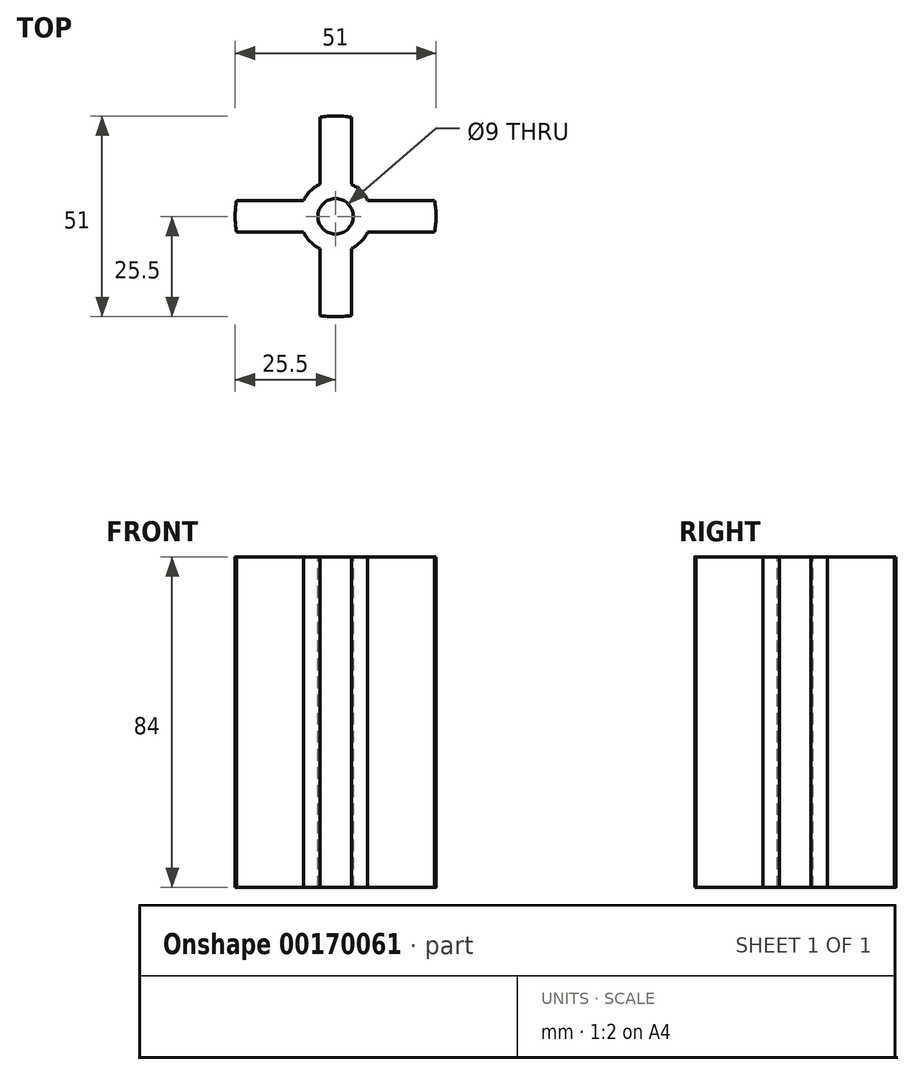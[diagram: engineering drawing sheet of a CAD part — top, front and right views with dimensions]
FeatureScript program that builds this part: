
annotation { "Feature Type Name" : "Feature", "Feature Type Description" : "" }
export const myFeature = defineFeature(function(context is Context, id is Id, definition is map)
    precondition{}
    {
        {
            var Q0;
            Q0=qCreatedBy(makeId("Top.planeOp"),FACE);
            var sketch = newSketch(context, id + "F0", { "sketchPlane" : qUnion([Q0])});
            skCircle(sketch, "E0", {"center": v(0, 0) * mm, "radius": 11.1 * mm});
            skCircle(sketch, "E1.0", {"center": v(0, 0) * mm, "radius": 13.1 * mm});
            skCircle(sketch, "E2.0", {"center": v(0, 0) * mm, "radius": 9.1 * mm});
            skCircle(sketch, "E3", {"center": v(0, 0) * mm, "radius": 25.5 * mm});
            skLineSegment(sketch, "E4.bottom", {"start": v(-4, -25.18) * mm, "end": v(4, -25.18) * mm});
            skLineSegment(sketch, "E4.top", {"start": v(-4, 25.18) * mm, "end": v(4, 25.18) * mm});
            skLineSegment(sketch, "E4.left", {"start": v(-4, -25.18) * mm, "end": v(-4, 25.18) * mm});
            skLineSegment(sketch, "E4.right", {"start": v(4, -25.18) * mm, "end": v(4, 25.18) * mm});
            skLineSegment(sketch, "E5.bottom", {"start": v(-25.18, -4) * mm, "end": v(25.18, -4) * mm});
            skLineSegment(sketch, "E5.top", {"start": v(-25.18, 4) * mm, "end": v(25.18, 4) * mm});
            skLineSegment(sketch, "E5.left", {"start": v(-25.18, -4) * mm, "end": v(-25.18, 4) * mm});
            skLineSegment(sketch, "E5.right", {"start": v(25.18, -4) * mm, "end": v(25.18, 4) * mm});
            skCircle(sketch, "E6", {"center": v(0, 0) * mm, "radius": 4.5 * mm});
            skSolve(sketch);
        }
        {
            var Q0;
            {var subQ5=sQuery(id+"F0.wireOp",EDGE,"E4.top");Q0=makeQuery(id+"F0.imprint","IMPRINT",FACE,{"disambiguationData":[TD([[makeQuery(id+"F0.imprint","IMPRINT",EDGE,{"derivedFrom":subQ5}),-1.0]])]});}
            var Q1;
            {var subQ0=sQuery(id+"F0.wireOp",EDGE,"E4.top");Q1=makeQuery(id+"F0.imprint","IMPRINT",FACE,{"disambiguationData":[TD([[makeQuery(id+"F0.imprint","IMPRINT",EDGE,{"derivedFrom":subQ0}),1.0]])]});}
            var Q2;
            {var subQ0=sQuery(id+"F0.wireOp",EDGE,"E5.right");Q2=makeQuery(id+"F0.imprint","IMPRINT",FACE,{"disambiguationData":[TD([[makeQuery(id+"F0.imprint","IMPRINT",EDGE,{"derivedFrom":subQ0}),-1.0]])]});}
            var Q3;
            {var subQ5=sQuery(id+"F0.wireOp",EDGE,"E5.right");Q3=makeQuery(id+"F0.imprint","IMPRINT",FACE,{"disambiguationData":[TD([[makeQuery(id+"F0.imprint","IMPRINT",EDGE,{"derivedFrom":subQ5}),1.0]])]});}
            var Q4;
            {var subQ0=sQuery(id+"F0.wireOp",EDGE,"E4.bottom");Q4=makeQuery(id+"F0.imprint","IMPRINT",FACE,{"disambiguationData":[TD([[makeQuery(id+"F0.imprint","IMPRINT",EDGE,{"derivedFrom":subQ0}),-1.0]])]});}
            var Q5;
            {var subQ0=sQuery(id+"F0.wireOp",EDGE,"E5.left");Q5=makeQuery(id+"F0.imprint","IMPRINT",FACE,{"disambiguationData":[TD([[makeQuery(id+"F0.imprint","IMPRINT",EDGE,{"derivedFrom":subQ0}),1.0]])]});}
            var Q6;
            {var subQ5=sQuery(id+"F0.wireOp",EDGE,"E5.left");Q6=makeQuery(id+"F0.imprint","IMPRINT",FACE,{"disambiguationData":[TD([[makeQuery(id+"F0.imprint","IMPRINT",EDGE,{"derivedFrom":subQ5}),-1.0]])]});}
            var Q7;
            {var subQ5=sQuery(id+"F0.wireOp",EDGE,"E4.bottom");Q7=makeQuery(id+"F0.imprint","IMPRINT",FACE,{"disambiguationData":[TD([[makeQuery(id+"F0.imprint","IMPRINT",EDGE,{"derivedFrom":subQ5}),1.0]])]});}
            var Q8;
            {var subQ0=sQuery(id+"F0.wireOp",EDGE,"E5.top");var subQ1=sQuery(id+"F0.wireOp",EDGE,"E0");var subQ2=makeQuery(id+"F0.imprint","INTERSECT",VERTEX,{"disambiguationData":[OD(1.0)],"derivedFrom":[subQ1,subQ0]});Q8=makeQuery(id+"F0.imprint","IMPRINT",FACE,{"disambiguationData":[TD([[makeQuery(id+"F0.imprint","IMPRINT",EDGE,{"disambiguationData":[TD([[subQ2,-1.0]])],"derivedFrom":subQ1}),1.0]])]});}
            var Q9;
            {var subQ0=sQuery(id+"F0.wireOp",EDGE,"E5.top");var subQ1=sQuery(id+"F0.wireOp",EDGE,"E0");var subQ2=makeQuery(id+"F0.imprint","INTERSECT",VERTEX,{"disambiguationData":[OD(1.0)],"derivedFrom":[subQ1,subQ0]});Q9=makeQuery(id+"F0.imprint","IMPRINT",FACE,{"disambiguationData":[TD([[makeQuery(id+"F0.imprint","IMPRINT",EDGE,{"disambiguationData":[TD([[subQ2,-1.0]])],"derivedFrom":subQ1}),-1.0]])]});}
            var Q10;
            {var subQ0=sQuery(id+"F0.wireOp",EDGE,"E4.right");var subQ1=sQuery(id+"F0.wireOp",EDGE,"E0");var subQ2=makeQuery(id+"F0.imprint","INTERSECT",VERTEX,{"disambiguationData":[OD(0.0)],"derivedFrom":[subQ1,subQ0]});Q10=makeQuery(id+"F0.imprint","IMPRINT",FACE,{"disambiguationData":[TD([[makeQuery(id+"F0.imprint","IMPRINT",EDGE,{"disambiguationData":[TD([[subQ2,-1.0]])],"derivedFrom":subQ1}),1.0]])]});}
            var Q11;
            {var subQ0=sQuery(id+"F0.wireOp",EDGE,"E4.right");var subQ1=sQuery(id+"F0.wireOp",EDGE,"E0");var subQ2=makeQuery(id+"F0.imprint","INTERSECT",VERTEX,{"disambiguationData":[OD(0.0)],"derivedFrom":[subQ1,subQ0]});Q11=makeQuery(id+"F0.imprint","IMPRINT",FACE,{"disambiguationData":[TD([[makeQuery(id+"F0.imprint","IMPRINT",EDGE,{"disambiguationData":[TD([[subQ2,-1.0]])],"derivedFrom":subQ1}),-1.0]])]});}
            var Q12;
            {var subQ0=sQuery(id+"F0.wireOp",EDGE,"E5.top");var subQ1=sQuery(id+"F0.wireOp",EDGE,"E0");var subQ2=makeQuery(id+"F0.imprint","INTERSECT",VERTEX,{"disambiguationData":[OD(0.0)],"derivedFrom":[subQ1,subQ0]});Q12=makeQuery(id+"F0.imprint","IMPRINT",FACE,{"disambiguationData":[TD([[makeQuery(id+"F0.imprint","IMPRINT",EDGE,{"disambiguationData":[TD([[subQ2,1.0]])],"derivedFrom":subQ1}),-1.0]])]});}
            var Q13;
            {var subQ0=sQuery(id+"F0.wireOp",EDGE,"E5.top");var subQ1=sQuery(id+"F0.wireOp",EDGE,"E0");var subQ2=makeQuery(id+"F0.imprint","INTERSECT",VERTEX,{"disambiguationData":[OD(0.0)],"derivedFrom":[subQ1,subQ0]});Q13=makeQuery(id+"F0.imprint","IMPRINT",FACE,{"disambiguationData":[TD([[makeQuery(id+"F0.imprint","IMPRINT",EDGE,{"disambiguationData":[TD([[subQ2,1.0]])],"derivedFrom":subQ1}),1.0]])]});}
            var Q14;
            {var subQ0=sQuery(id+"F0.wireOp",EDGE,"E4.left");var subQ1=sQuery(id+"F0.wireOp",EDGE,"E0");var subQ2=makeQuery(id+"F0.imprint","INTERSECT",VERTEX,{"disambiguationData":[OD(1.0)],"derivedFrom":[subQ1,subQ0]});Q14=makeQuery(id+"F0.imprint","IMPRINT",FACE,{"disambiguationData":[TD([[makeQuery(id+"F0.imprint","IMPRINT",EDGE,{"disambiguationData":[TD([[subQ2,-1.0]])],"derivedFrom":subQ1}),1.0]])]});}
            var Q15;
            {var subQ0=sQuery(id+"F0.wireOp",EDGE,"E4.left");var subQ1=sQuery(id+"F0.wireOp",EDGE,"E0");var subQ2=makeQuery(id+"F0.imprint","INTERSECT",VERTEX,{"disambiguationData":[OD(1.0)],"derivedFrom":[subQ1,subQ0]});Q15=makeQuery(id+"F0.imprint","IMPRINT",FACE,{"disambiguationData":[TD([[makeQuery(id+"F0.imprint","IMPRINT",EDGE,{"disambiguationData":[TD([[subQ2,-1.0]])],"derivedFrom":subQ1}),-1.0]])]});}
            var Q16;
            {var subQ3=sQuery(id+"F0.wireOp",EDGE,"E5.top");var subQ8=sQuery(id+"F0.wireOp",EDGE,"E2.0");var subQ10=makeQuery(id+"F0.imprint","INTERSECT",VERTEX,{"disambiguationData":[OD(1.0)],"derivedFrom":[subQ8,subQ3]});Q16=makeQuery(id+"F0.imprint","IMPRINT",FACE,{"disambiguationData":[TD([[makeQuery(id+"F0.imprint","IMPRINT",EDGE,{"disambiguationData":[TD([[subQ10,-1.0]])],"derivedFrom":subQ8}),1.0]])]});}
            var Q17;
            {var subQ0=sQuery(id+"F0.wireOp",EDGE,"E4.left");var subQ1=sQuery(id+"F0.wireOp",EDGE,"E2.0");var subQ2=makeQuery(id+"F0.imprint","INTERSECT",VERTEX,{"disambiguationData":[OD(0.0)],"derivedFrom":[subQ1,subQ0]});Q17=makeQuery(id+"F0.imprint","IMPRINT",FACE,{"disambiguationData":[TD([[makeQuery(id+"F0.imprint","IMPRINT",EDGE,{"disambiguationData":[TD([[subQ2,-1.0]])],"derivedFrom":subQ1}),1.0]])]});}
            var Q18;
            {var subQ5=sQuery(id+"F0.wireOp",EDGE,"E2.0");var subQ7=sQuery(id+"F0.wireOp",EDGE,"E4.right");var subQ8=makeQuery(id+"F0.imprint","INTERSECT",VERTEX,{"disambiguationData":[OD(0.0)],"derivedFrom":[subQ5,subQ7]});Q18=makeQuery(id+"F0.imprint","IMPRINT",FACE,{"disambiguationData":[TD([[makeQuery(id+"F0.imprint","IMPRINT",EDGE,{"disambiguationData":[TD([[subQ8,-1.0]])],"derivedFrom":subQ5}),1.0]])]});}
            var Q19;
            {var subQ0=sQuery(id+"F0.wireOp",EDGE,"E4.right");var subQ1=sQuery(id+"F0.wireOp",EDGE,"E2.0");var subQ2=makeQuery(id+"F0.imprint","INTERSECT",VERTEX,{"disambiguationData":[OD(0.0)],"derivedFrom":[subQ1,subQ0]});Q19=makeQuery(id+"F0.imprint","IMPRINT",FACE,{"disambiguationData":[TD([[makeQuery(id+"F0.imprint","IMPRINT",EDGE,{"disambiguationData":[TD([[subQ2,1.0]])],"derivedFrom":subQ1}),1.0]])]});}
            var Q20;
            {var subQ3=sQuery(id+"F0.wireOp",EDGE,"E5.top");var subQ8=sQuery(id+"F0.wireOp",EDGE,"E2.0");var subQ10=makeQuery(id+"F0.imprint","INTERSECT",VERTEX,{"disambiguationData":[OD(0.0)],"derivedFrom":[subQ8,subQ3]});Q20=makeQuery(id+"F0.imprint","IMPRINT",FACE,{"disambiguationData":[TD([[makeQuery(id+"F0.imprint","IMPRINT",EDGE,{"disambiguationData":[TD([[subQ10,1.0]])],"derivedFrom":subQ8}),1.0]])]});}
            var Q21;
            {var subQ1=sQuery(id+"F0.wireOp",EDGE,"E4.left");var subQ6=sQuery(id+"F0.wireOp",EDGE,"E2.0");var subQ9=makeQuery(id+"F0.imprint","INTERSECT",VERTEX,{"disambiguationData":[OD(1.0)],"derivedFrom":[subQ6,subQ1]});Q21=makeQuery(id+"F0.imprint","IMPRINT",FACE,{"disambiguationData":[TD([[makeQuery(id+"F0.imprint","IMPRINT",EDGE,{"disambiguationData":[TD([[subQ9,-1.0]])],"derivedFrom":subQ6}),1.0]])]});}
            var Q22;
            {var subQ0=sQuery(id+"F0.wireOp",EDGE,"E5.bottom");var subQ1=sQuery(id+"F0.wireOp",EDGE,"E2.0");var subQ2=makeQuery(id+"F0.imprint","INTERSECT",VERTEX,{"disambiguationData":[OD(0.0)],"derivedFrom":[subQ1,subQ0]});Q22=makeQuery(id+"F0.imprint","IMPRINT",FACE,{"disambiguationData":[TD([[makeQuery(id+"F0.imprint","IMPRINT",EDGE,{"disambiguationData":[TD([[subQ2,-1.0]])],"derivedFrom":subQ1}),1.0]])]});}
            var Q23;
            {var subQ0=sQuery(id+"F0.wireOp",EDGE,"E4.right");var subQ1=sQuery(id+"F0.wireOp",EDGE,"E2.0");var subQ2=makeQuery(id+"F0.imprint","INTERSECT",VERTEX,{"disambiguationData":[OD(1.0)],"derivedFrom":[subQ1,subQ0]});Q23=makeQuery(id+"F0.imprint","IMPRINT",FACE,{"disambiguationData":[TD([[makeQuery(id+"F0.imprint","IMPRINT",EDGE,{"disambiguationData":[TD([[subQ2,-1.0]])],"derivedFrom":subQ1}),1.0]])]});}
            var Q24;
            {var subQ0=sQuery(id+"F0.wireOp",EDGE,"E5.bottom");var subQ1=sQuery(id+"F0.wireOp",EDGE,"E4.right");var subQ2=makeQuery(id+"F0.imprint","INTERSECT",VERTEX,{"derivedFrom":[subQ1,subQ0]});Q24=makeQuery(id+"F0.imprint","IMPRINT",FACE,{"disambiguationData":[TD([[makeQuery(id+"F0.imprint","IMPRINT",EDGE,{"disambiguationData":[TD([[subQ2,-1.0]])],"derivedFrom":subQ1}),1.0]])]});}
            var Q25;
            {var subQ0=sQuery(id+"F0.wireOp",EDGE,"E5.bottom");var subQ1=sQuery(id+"F0.wireOp",EDGE,"E4.left");var subQ2=makeQuery(id+"F0.imprint","INTERSECT",VERTEX,{"derivedFrom":[subQ1,subQ0]});Q25=makeQuery(id+"F0.imprint","IMPRINT",FACE,{"disambiguationData":[TD([[makeQuery(id+"F0.imprint","IMPRINT",EDGE,{"disambiguationData":[TD([[subQ2,-1.0]])],"derivedFrom":subQ1}),-1.0]])]});}
            var Q26;
            {var subQ0=sQuery(id+"F0.wireOp",EDGE,"E6");var subQ1=sQuery(id+"F0.wireOp",EDGE,"E4.left");var subQ2=makeQuery(id+"F0.imprint","INTERSECT",VERTEX,{"disambiguationData":[OD(1.0)],"derivedFrom":[subQ1,subQ0]});Q26=makeQuery(id+"F0.imprint","IMPRINT",FACE,{"disambiguationData":[TD([[makeQuery(id+"F0.imprint","IMPRINT",EDGE,{"disambiguationData":[TD([[subQ2,-1.0]])],"derivedFrom":subQ1}),-1.0]])]});}
            var Q27;
            {var subQ0=sQuery(id+"F0.wireOp",EDGE,"E6");var subQ1=sQuery(id+"F0.wireOp",EDGE,"E4.right");var subQ2=makeQuery(id+"F0.imprint","INTERSECT",VERTEX,{"disambiguationData":[OD(1.0)],"derivedFrom":[subQ1,subQ0]});Q27=makeQuery(id+"F0.imprint","IMPRINT",FACE,{"disambiguationData":[TD([[makeQuery(id+"F0.imprint","IMPRINT",EDGE,{"disambiguationData":[TD([[subQ2,-1.0]])],"derivedFrom":subQ1}),1.0]])]});}
            extrude(context, id + "F1", {"entities" : qUnion([Q0, Q1, Q2, Q3, Q4, Q5, Q6, Q7, Q8, Q9, Q10, Q11, Q12, Q13, Q14, Q15, Q16, Q17, Q18, Q19, Q20, Q21, Q22, Q23, Q24, Q25, Q26, Q27]), "flatOperationType" : FlatOperationType.REMOVE, "oppositeDirection" : true, "offsetDistance" : 25 * mm, "depth" : 84 * mm, "domain" : OperationDomain.MODEL});
        }
    });
